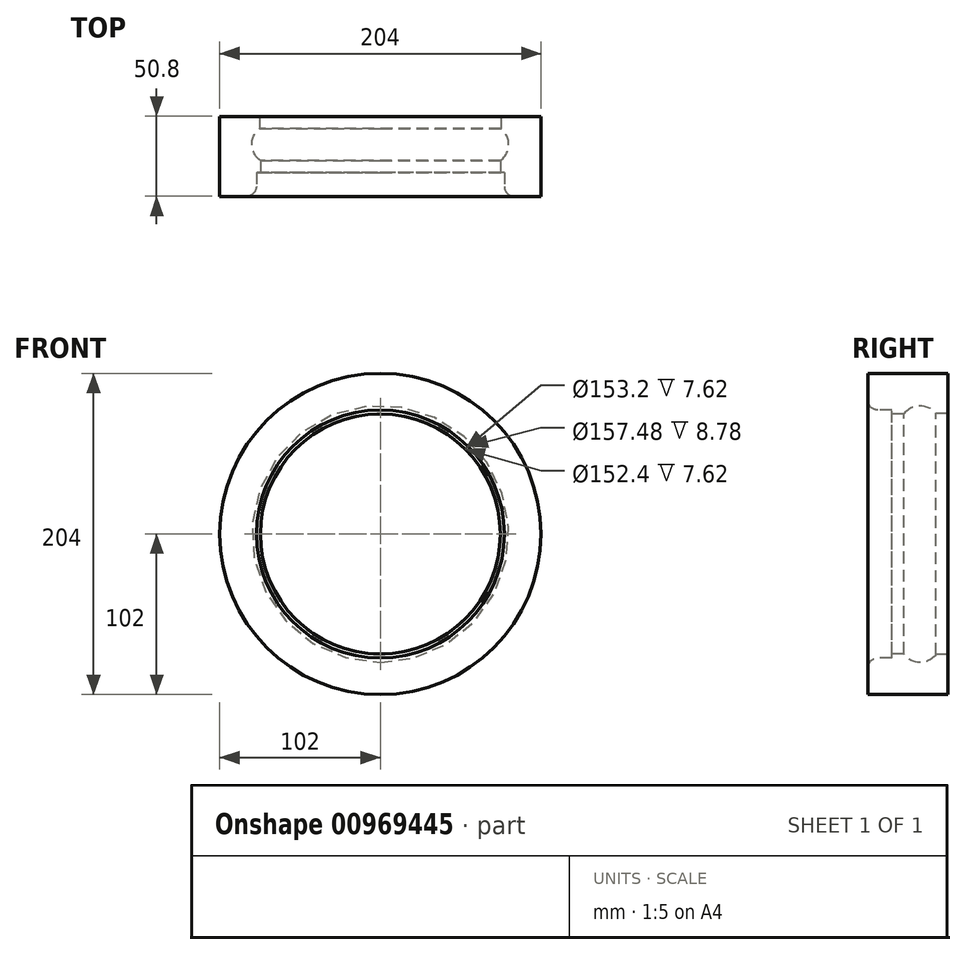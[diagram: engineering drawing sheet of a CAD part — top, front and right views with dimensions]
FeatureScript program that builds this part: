
annotation { "Feature Type Name" : "Feature", "Feature Type Description" : "" }
export const myFeature = defineFeature(function(context is Context, id is Id, definition is map)
    precondition{}
    {
        {
            var Q0;
            Q0=qCreatedBy(makeId("Right.planeOp"),FACE);
            var sketch = newSketch(context, id + "F0", { "sketchPlane" : qUnion([Q0])});
            skLineSegment(sketch, "E0", {"start": v(-27, 102) * mm, "end": v(23.8, 102) * mm});
            skLineSegment(sketch, "E1", {"start": v(23.8, 102) * mm, "end": v(23.8, 76.6) * mm});
            skLineSegment(sketch, "E2", {"start": v(23.8, 76.6) * mm, "end": v(16.18, 76.6) * mm});
            skLineSegment(sketch, "E3", {"start": v(-27, 102) * mm, "end": v(-27, 85.09) * mm});
            skLineSegment(sketch, "E4", {"start": v(-20.65, 78.74) * mm, "end": v(-11.87, 78.74) * mm});
            skLineSegment(sketch, "E5", {"start": v(-11.87, 76.2) * mm, "end": v(-11.87, 78.74) * mm});
            skLineSegment(sketch, "E6", {"start": v(-11.87, 76.2) * mm, "end": v(-4.25, 76.2) * mm});
            skArc(sketch, "E7", {"start": v(16.18, 76.6) * mm, "mid": v(5.86, 81.56) * mm, "end": v(-4.25, 76.2) * mm});
            skPoint(sketch, "E8.visualSharp", {"position": v(-27, 78.74) * mm});
            skArc(sketch, "E8.filletArc", {"start": v(-27, 85.09) * mm, "mid": v(-25.14, 80.6) * mm, "end": v(-20.65, 78.74) * mm});
            skLineSegment(sketch, "E9", {"start": v(-71.3, 0) * mm, "end": v(65.64, 0) * mm});
            skSolve(sketch);
        }
        {
            var Q0;
            Q0=makeQuery(id+"F0.imprint","IMPRINT",FACE,{"disambiguationData":[TD([[makeQuery(id+"F0.imprint","IMPRINT",EDGE,{"derivedFrom":sQuery(id+"F0.wireOp",EDGE,"E0")}),-1.0]])]});
            var Q1;
            Q1=sQuery(id+"F0.wireOp",EDGE,"E9");
            revolve(context, id + "F1", {"surfaceOperationType" : NewSurfaceOperationType.NEW, "entities" : qUnion([Q0]), "axis" : qUnion([Q1]), "revolveType" : RevolveType.FULL});
        }
    });
